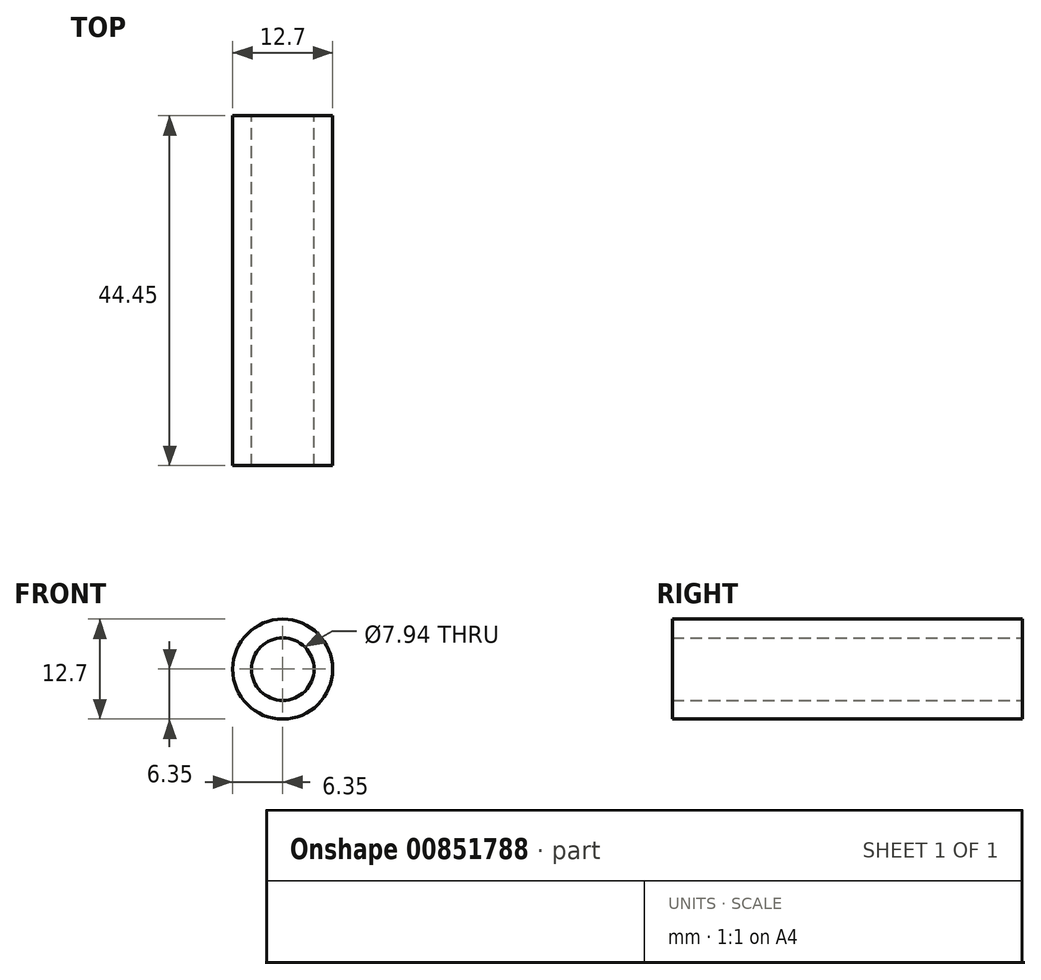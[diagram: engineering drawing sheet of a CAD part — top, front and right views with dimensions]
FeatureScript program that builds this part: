
annotation { "Feature Type Name" : "Feature", "Feature Type Description" : "" }
export const myFeature = defineFeature(function(context is Context, id is Id, definition is map)
    precondition{}
    {
        {
            var Q0;
            Q0=qCreatedBy(makeId("Front.planeOp"),FACE);
            var sketch = newSketch(context, id + "F0", { "sketchPlane" : qUnion([Q0])});
            skCircle(sketch, "E0", {"center": v(0, 0) * mm, "radius": 6.35 * mm});
            skCircle(sketch, "E1", {"center": v(0, 0) * mm, "radius": 3.97 * mm});
            skSolve(sketch);
        }
        {
            var Q0;
            Q0=makeQuery(id+"F0.imprint","IMPRINT",FACE,{"disambiguationData":[TD([[makeQuery(id+"F0.imprint","IMPRINT",EDGE,{"derivedFrom":sQuery(id+"F0.wireOp",EDGE,"E0")}),1.0]])]});
            extrude(context, id + "F1", {"entities" : qUnion([Q0]), "depth" : 44.45 * mm, "offsetDistance" : 25.4 * mm});
        }
    });
